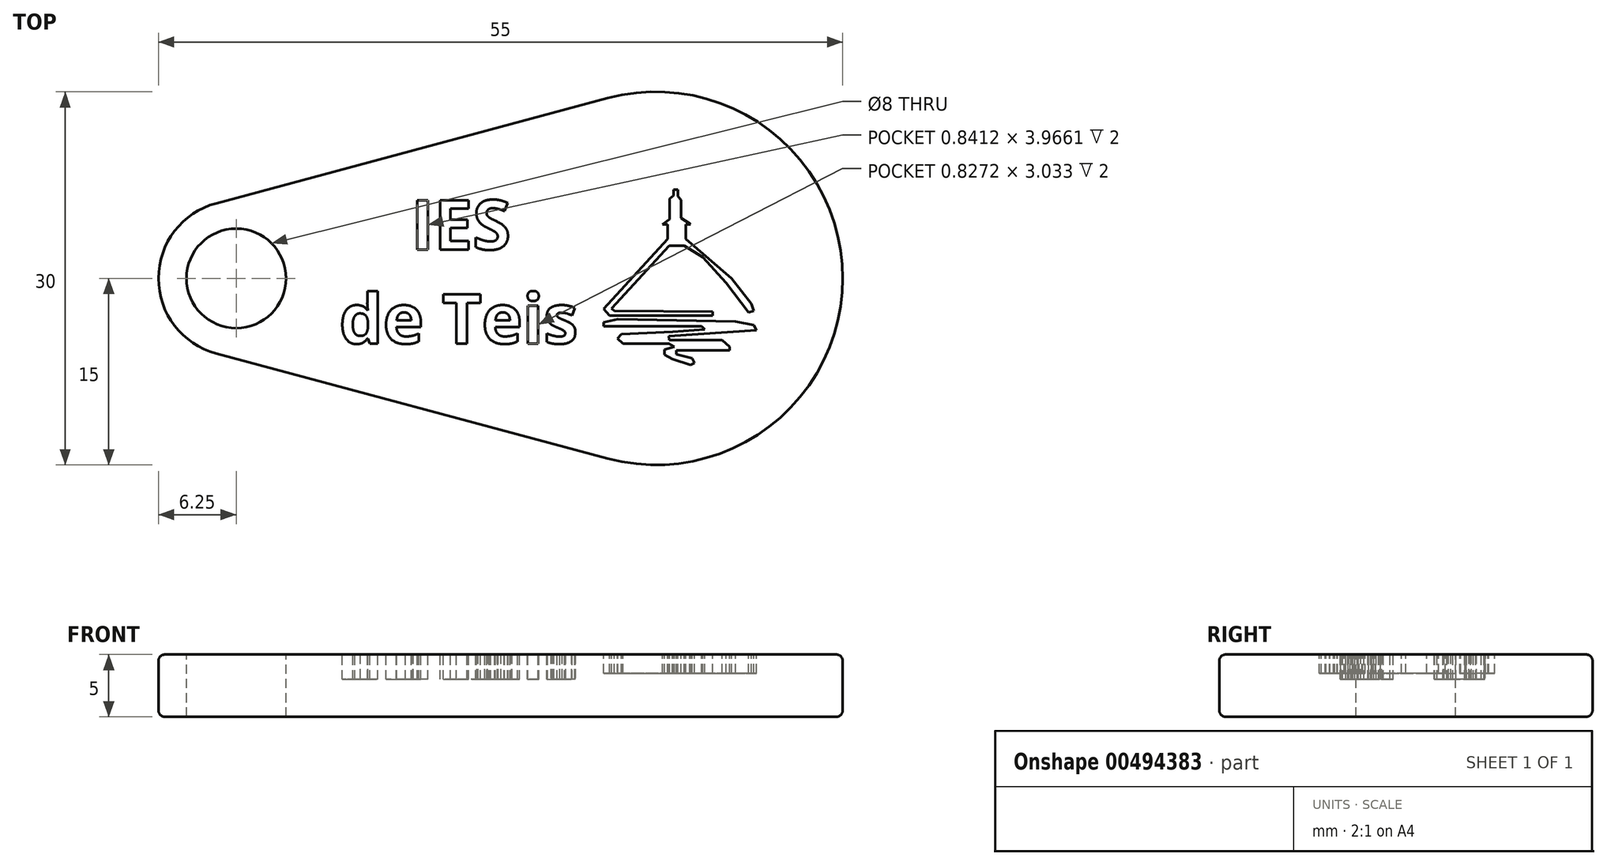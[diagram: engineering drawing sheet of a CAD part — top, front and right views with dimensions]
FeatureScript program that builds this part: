
annotation { "Feature Type Name" : "Feature", "Feature Type Description" : "" }
export const myFeature = defineFeature(function(context is Context, id is Id, definition is map)
    precondition{}
    {
        {
            var Q0;
            Q0=qCreatedBy(makeId("Top.planeOp"),FACE);
            var sketch = newSketch(context, id + "F0", { "sketchPlane" : qUnion([Q0])});
            skCircle(sketch, "E0", {"center": v(-33.75, 0) * mm, "radius": 6.25 * mm});
            skCircle(sketch, "E1", {"center": v(0, 0) * mm, "radius": 15 * mm});
            skLineSegment(sketch, "E2", {"start": v(-35.37, 6.04) * mm, "end": v(-3.89, 14.49) * mm});
            skLineSegment(sketch, "E3", {"start": v(-35.37, -6.04) * mm, "end": v(-3.89, -14.49) * mm});
            skSolve(sketch);
        }
        {
            var Q0;
            {var subQ0=sQuery(id+"F0.wireOp",EDGE,"E0");var subQ1=makeQuery(id+"F0.imprint","INTERSECT",VERTEX,{"derivedFrom":[subQ0,sQuery(id+"F0.wireOp",EDGE,"E2")]});Q0=makeQuery(id+"F0.imprint","IMPRINT",FACE,{"disambiguationData":[TD([[makeQuery(id+"F0.imprint","IMPRINT",EDGE,{"disambiguationData":[TD([[subQ1,-1.0]])],"derivedFrom":subQ0}),1.0]])]});}
            var Q1;
            {var subQ0=sQuery(id+"F0.wireOp",EDGE,"E2");Q1=makeQuery(id+"F0.imprint","IMPRINT",FACE,{"disambiguationData":[TD([[makeQuery(id+"F0.imprint","IMPRINT",EDGE,{"derivedFrom":subQ0}),-1.0]])]});}
            var Q2;
            {var subQ0=sQuery(id+"F0.wireOp",EDGE,"E1");var subQ1=makeQuery(id+"F0.imprint","INTERSECT",VERTEX,{"derivedFrom":[subQ0,sQuery(id+"F0.wireOp",EDGE,"E2")]});Q2=makeQuery(id+"F0.imprint","IMPRINT",FACE,{"disambiguationData":[TD([[makeQuery(id+"F0.imprint","IMPRINT",EDGE,{"disambiguationData":[TD([[subQ1,-1.0]])],"derivedFrom":subQ0}),1.0]])]});}
            extrude(context, id + "F1", {"entities" : qUnion([Q0, Q1, Q2]), "depth" : 5 * mm});
        }
        {
            var Q0;
            Q0=makeQuery(id+"F1.opExtrude","CAP_FACE",FACE,{"disambiguationData":[OSD([sQuery(id+"F0.wireOp",EDGE,"E0"),sQuery(id+"F0.wireOp",EDGE,"E1"),sQuery(id+"F0.wireOp",EDGE,"E2"),sQuery(id+"F0.wireOp",EDGE,"E3")])],"isStart":false});
            var sketch = newSketch(context, id + "F2", { "sketchPlane" : qUnion([Q0])});
            skCircle(sketch, "E4", {"center": v(-33.75, 0) * mm, "radius": 4 * mm});
            skSolve(sketch);
        }
        {
            var Q0;
            Q0=makeQuery(id+"F1.opExtrude","CAP_EDGE",EDGE,{"disambiguationData":[OSD([sQuery(id+"F0.wireOp",EDGE,"E2")])],"isStart":false});
            var Q1;
            Q1=makeQuery(id+"F1.opExtrude","CAP_EDGE",EDGE,{"disambiguationData":[OSD([sQuery(id+"F0.wireOp",EDGE,"E0")])],"isStart":false});
            var Q2;
            Q2=makeQuery(id+"F1.opExtrude","CAP_EDGE",EDGE,{"disambiguationData":[OSD([sQuery(id+"F0.wireOp",EDGE,"E3")])],"isStart":false});
            var Q3;
            Q3=makeQuery(id+"F1.opExtrude","CAP_EDGE",EDGE,{"disambiguationData":[OSD([sQuery(id+"F0.wireOp",EDGE,"E1")])],"isStart":false});
            var Q4;
            Q4=makeQuery(id+"F4.boolean.opBoolean","COPY",EDGE,{"derivedFrom":makeQuery(id+"F4.opExtrude","CAP_EDGE",EDGE,{"disambiguationData":[OSD([sQuery(id+"F2.wireOp",EDGE,"E4")])],"isStart":true})});
            var Q5;
            Q5=makeQuery(id+"F1.opExtrude","CAP_EDGE",EDGE,{"disambiguationData":[OSD([sQuery(id+"F0.wireOp",EDGE,"E2")])],"isStart":true});
            var Q6;
            Q6=makeQuery(id+"F1.opExtrude","CAP_EDGE",EDGE,{"disambiguationData":[OSD([sQuery(id+"F0.wireOp",EDGE,"E0")])],"isStart":true});
            var Q7;
            Q7=makeQuery(id+"F1.opExtrude","CAP_EDGE",EDGE,{"disambiguationData":[OSD([sQuery(id+"F0.wireOp",EDGE,"E3")])],"isStart":true});
            var Q8;
            Q8=makeQuery(id+"F1.opExtrude","CAP_EDGE",EDGE,{"disambiguationData":[OSD([sQuery(id+"F0.wireOp",EDGE,"E1")])],"isStart":true});
            var Q9;
            Q9=makeQuery(id+"F4.boolean.opBoolean","INTERSECT",EDGE,{"derivedFrom":[makeQuery(id+"F1.opExtrude","CAP_FACE",FACE,{"disambiguationData":[OSD([sQuery(id+"F0.wireOp",EDGE,"E0"),sQuery(id+"F0.wireOp",EDGE,"E1"),sQuery(id+"F0.wireOp",EDGE,"E2"),sQuery(id+"F0.wireOp",EDGE,"E3")])],"isStart":true}),makeQuery(id+"F4.opExtrude","SWEPT_FACE",FACE,{"disambiguationData":[OSD([sQuery(id+"F2.wireOp",EDGE,"E4")])]})]});
            fillet(context, id + "F3", {"entities" : qUnion([Q0, Q1, Q2, Q3, Q4, Q5, Q6, Q7, Q8, Q9]), "radius" : 0.5 * mm, "tangentPropagation" : true, "allowEdgeOverflow" : false});
        }
        {
            var Q0;
            Q0=makeQuery(id+"F2.imprint","IMPRINT",FACE,{"disambiguationData":[TD([[makeQuery(id+"F2.imprint","IMPRINT",EDGE,{"derivedFrom":sQuery(id+"F2.wireOp",EDGE,"E4")}),1.0]])]});
            extrude(context, id + "F4", {"entities" : qUnion([Q0]), "operationType" : NewBodyOperationType.REMOVE, "oppositeDirection" : true, "depth" : 25 * mm});
        }
        {
            var Q0;
            Q0=makeQuery(id+"F1.opExtrude","CAP_FACE",FACE,{"disambiguationData":[OSD([sQuery(id+"F0.wireOp",EDGE,"E0"),sQuery(id+"F0.wireOp",EDGE,"E1"),sQuery(id+"F0.wireOp",EDGE,"E2"),sQuery(id+"F0.wireOp",EDGE,"E3")])],"isStart":false});
            var sketch = newSketch(context, id + "F5", { "sketchPlane" : qUnion([Q0])});
            skLineSegment(sketch, "E5", {"start": v(4.56, -2.67) * mm, "end": v(4.56, -3) * mm});
            skLineSegment(sketch, "E6", {"start": v(4.56, -3) * mm, "end": v(-3.75, -3) * mm});
            skLineSegment(sketch, "E7", {"start": v(-3.75, -3) * mm, "end": v(-4.2, -2.45) * mm});
            skLineSegment(sketch, "E8", {"start": v(-4.2, -2.45) * mm, "end": v(0.92, 3.17) * mm});
            skLineSegment(sketch, "E9", {"start": v(0.92, 3.17) * mm, "end": v(2.4, 3.17) * mm});
            skLineSegment(sketch, "E10", {"start": v(2.4, 3.17) * mm, "end": v(6.07, 0) * mm});
            skLineSegment(sketch, "E11", {"start": v(6.07, 0) * mm, "end": v(7.67, -2.05) * mm});
            skLineSegment(sketch, "E12", {"start": v(7.67, -2.05) * mm, "end": v(7.86, -2.62) * mm});
            skLineSegment(sketch, "E13", {"start": v(7.86, -2.62) * mm, "end": v(7.45, -2.76) * mm});
            skLineSegment(sketch, "E14", {"start": v(7.45, -2.76) * mm, "end": v(5.61, -0.35) * mm});
            skLineSegment(sketch, "E15", {"start": v(5.61, -0.35) * mm, "end": v(3.75, 1.69) * mm});
            skLineSegment(sketch, "E16", {"start": v(3.75, 1.69) * mm, "end": v(2.26, 2.62) * mm});
            skLineSegment(sketch, "E17", {"start": v(2.26, 2.62) * mm, "end": v(1.06, 2.62) * mm});
            skLineSegment(sketch, "E18", {"start": v(1.06, 2.62) * mm, "end": v(-3.58, -2.43) * mm});
            skLineSegment(sketch, "E19", {"start": v(-3.58, -2.43) * mm, "end": v(-3.37, -2.62) * mm});
            skLineSegment(sketch, "E20", {"start": v(-3.37, -2.62) * mm, "end": v(4.56, -2.67) * mm});
            skLineSegment(sketch, "E21", {"start": v(-4.23, -3.53) * mm, "end": v(-3.08, -3.3) * mm});
            skLineSegment(sketch, "E22", {"start": v(-3.08, -3.3) * mm, "end": v(6.4, -3.48) * mm});
            skLineSegment(sketch, "E23", {"start": v(6.4, -3.48) * mm, "end": v(7.86, -3.77) * mm});
            skLineSegment(sketch, "E24", {"start": v(7.86, -3.77) * mm, "end": v(8.08, -4.18) * mm});
            skLineSegment(sketch, "E25", {"start": v(8.08, -4.18) * mm, "end": v(1.04, -4.66) * mm});
            skLineSegment(sketch, "E26", {"start": v(1.04, -4.66) * mm, "end": v(1.06, -4.97) * mm});
            skLineSegment(sketch, "E27", {"start": v(1.06, -4.97) * mm, "end": v(5.33, -4.97) * mm});
            skLineSegment(sketch, "E28", {"start": v(5.33, -4.97) * mm, "end": v(5.92, -5.5) * mm});
            skLineSegment(sketch, "E29", {"start": v(5.92, -5.5) * mm, "end": v(5.92, -5.8) * mm});
            skLineSegment(sketch, "E30", {"start": v(5.92, -5.8) * mm, "end": v(1.62, -5.8) * mm});
            skLineSegment(sketch, "E31", {"start": v(1.62, -5.8) * mm, "end": v(1.62, -6.1) * mm});
            skLineSegment(sketch, "E32", {"start": v(1.62, -6.1) * mm, "end": v(2.88, -6.43) * mm});
            skLineSegment(sketch, "E33", {"start": v(2.88, -6.43) * mm, "end": v(3.08, -6.81) * mm});
            skLineSegment(sketch, "E34", {"start": v(3.08, -6.81) * mm, "end": v(2.77, -6.96) * mm});
            skLineSegment(sketch, "E35", {"start": v(2.77, -6.96) * mm, "end": v(1.3, -6.5) * mm});
            skLineSegment(sketch, "E36", {"start": v(1.3, -6.5) * mm, "end": v(0.68, -6.14) * mm});
            skLineSegment(sketch, "E37", {"start": v(0.68, -6.14) * mm, "end": v(0.68, -5.73) * mm});
            skLineSegment(sketch, "E38", {"start": v(0.68, -5.73) * mm, "end": v(1.47, -5.52) * mm});
            skLineSegment(sketch, "E39", {"start": v(1.47, -5.52) * mm, "end": v(1.04, -5.25) * mm});
            skLineSegment(sketch, "E40", {"start": v(1.04, -5.25) * mm, "end": v(-2.65, -5.25) * mm});
            skLineSegment(sketch, "E41", {"start": v(-2.65, -5.25) * mm, "end": v(-3.1, -4.85) * mm});
            skLineSegment(sketch, "E42", {"start": v(-3.1, -4.85) * mm, "end": v(-2.8, -4.5) * mm});
            skLineSegment(sketch, "E43", {"start": v(-2.8, -4.5) * mm, "end": v(1.35, -4.3) * mm});
            skLineSegment(sketch, "E44", {"start": v(1.35, -4.3) * mm, "end": v(3.91, -4.1) * mm});
            skLineSegment(sketch, "E45", {"start": v(3.91, -4.1) * mm, "end": v(3.65, -3.84) * mm});
            skLineSegment(sketch, "E46", {"start": v(3.65, -3.84) * mm, "end": v(-3.46, -3.84) * mm});
            skLineSegment(sketch, "E47", {"start": v(-3.46, -3.84) * mm, "end": v(-4.23, -3.84) * mm});
            skLineSegment(sketch, "E48", {"start": v(-4.23, -3.84) * mm, "end": v(-4.23, -3.53) * mm});
            skLineSegment(sketch, "E49", {"start": v(2.4, 3.17) * mm, "end": v(2.4, 4.33) * mm});
            skLineSegment(sketch, "E50", {"start": v(2.4, 4.33) * mm, "end": v(2.76, 4.33) * mm});
            skLineSegment(sketch, "E51", {"start": v(2.76, 4.33) * mm, "end": v(2.7, 4.41) * mm});
            skLineSegment(sketch, "E52", {"start": v(2.7, 4.41) * mm, "end": v(2.03, 4.83) * mm});
            skLineSegment(sketch, "E53", {"start": v(2.03, 4.83) * mm, "end": v(2.03, 6.32) * mm});
            skLineSegment(sketch, "E54", {"start": v(1.74, 6.6) * mm, "end": v(1.74, 6.6) * mm});
            skLineSegment(sketch, "E55", {"start": v(1.74, 6.6) * mm, "end": v(1.74, 7.13) * mm});
            skLineSegment(sketch, "E56", {"start": v(1.74, 7.13) * mm, "end": v(1.4, 7.13) * mm});
            skLineSegment(sketch, "E57", {"start": v(1.4, 7.13) * mm, "end": v(1.4, 6.64) * mm});
            skLineSegment(sketch, "E58", {"start": v(1.4, 6.64) * mm, "end": v(1.08, 6.4) * mm});
            skLineSegment(sketch, "E59", {"start": v(1.08, 6.4) * mm, "end": v(1.08, 5.76) * mm});
            skLineSegment(sketch, "E60", {"start": v(1.08, 5.76) * mm, "end": v(1.08, 4.75) * mm});
            skLineSegment(sketch, "E61", {"start": v(1.08, 4.75) * mm, "end": v(0.53, 4.33) * mm});
            skLineSegment(sketch, "E62", {"start": v(0.53, 4.33) * mm, "end": v(0.92, 4.33) * mm});
            skLineSegment(sketch, "E63", {"start": v(0.92, 4.33) * mm, "end": v(0.92, 4.33) * mm});
            skLineSegment(sketch, "E64", {"start": v(0.92, 4.33) * mm, "end": v(0.92, 3.17) * mm});
            skLineSegment(sketch, "E65", {"start": v(2.03, 6.32) * mm, "end": v(1.74, 6.6) * mm});
            skSolve(sketch);
        }
        {
            var Q0;
            Q0=makeQuery(id+"F5.imprint","IMPRINT",FACE,{"disambiguationData":[TD([[makeQuery(id+"F5.imprint","IMPRINT",EDGE,{"derivedFrom":sQuery(id+"F5.wireOp",EDGE,"E5")}),-1.0]])]});
            var Q1;
            Q1=makeQuery(id+"F5.imprint","IMPRINT",FACE,{"disambiguationData":[TD([[makeQuery(id+"F5.imprint","IMPRINT",EDGE,{"derivedFrom":sQuery(id+"F5.wireOp",EDGE,"E21")}),-1.0]])]});
            var Q2;
            Q2=makeQuery(id+"F5.imprint","IMPRINT",FACE,{"disambiguationData":[TD([[makeQuery(id+"F5.imprint","IMPRINT",EDGE,{"derivedFrom":sQuery(id+"F5.wireOp",EDGE,"E9")}),1.0]])]});
            extrude(context, id + "F6", {"entities" : qUnion([Q0, Q1, Q2]), "operationType" : NewBodyOperationType.REMOVE, "oppositeDirection" : true, "depth" : 1.5 * mm});
        }
        {
            var Q0;
            Q0=makeQuery(id+"F1.opExtrude","CAP_FACE",FACE,{"disambiguationData":[OSD([sQuery(id+"F0.wireOp",EDGE,"E0"),sQuery(id+"F0.wireOp",EDGE,"E1"),sQuery(id+"F0.wireOp",EDGE,"E2"),sQuery(id+"F0.wireOp",EDGE,"E3")])],"isStart":false});
            var sketch = newSketch(context, id + "F7", { "sketchPlane" : qUnion([Q0])});
            skText(sketch, "E66", { "text": "    IES \nde Teis", "fontName": "OpenSans-Bold.ttf"});
            const initialGuessF7  = {"E66": [-0.02547, 0.00232, 1, 0, 0.004]};
            skSetInitialGuess(sketch, initialGuessF7);
            skSolve(sketch);
        }
        {
            var Q0;
            Q0 = qSketchRegion(id + "F7", true);
            extrude(context, id + "F8", {"entities" : qUnion([Q0]), "operationType" : NewBodyOperationType.REMOVE, "oppositeDirection" : true, "depth" : 2 * mm});
        }
    });
